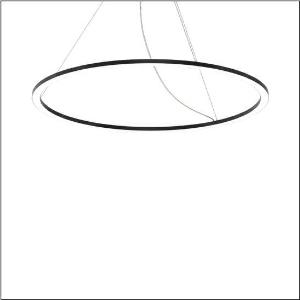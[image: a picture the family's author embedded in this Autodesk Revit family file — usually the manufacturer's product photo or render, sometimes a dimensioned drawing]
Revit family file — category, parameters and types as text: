
# Revit family: silica_r__21_ring-d_5pjbd4d1104a_1e9f
name_source: partatom
category: Lighting Fixtures
units: mm (PartAtom-declared; Revit-internal decimal feet)

## family parameters
Cut with Voids When Loaded = No
Host = Face
Light Source = No
Part Type = Normal
Room Calculation Point = No
Round Connector Dimension = Use Diameter
Shared = No

## types (1)
- Silica® 21 Ring-D (1 x LED, 10840 lm, 125 W, 3000K)
    Apparent Load = 125 VA
    CIE Flux Codes = 37 69 92 100 100
    Color Rendering = 80
    Color Temperature = 3000K
    Default Elevation = 1800 mm
    Description = Silica® 21 Ring-D, suspended luminaire, of PMMA, frosted, light emission: ring underside luminous distribution, primary light characteristic: symmetric, installation type: suspended mounting, LED, rated luminous flux: 10.840lm, luminous efficacy: 87lm/W, light colour: 830, colour temperature: 3000K, with terminal, 5-pole, mains connection: 230V, AC/DC, 0/50..60Hz, rated input power: 125W, housing, of extruded aluminium section, jet black (RAL 9005), diameter: 1.450mm, ceiling canopy, jet black (RAL 9005), protection rating (lamp compartment): IP40, insulation class (complete): insulation class I (protective earthing), certification: CE, impact resistance: IK02, permissible operating ambient temperature: 0..+35°C, packaging unit: 1 piece
    Height = 25 mm  [stored 0.082021 ft]
    Lamp = 1 x LED
    Lamp Light Flux = 10840 lm
    Lamp Power = 125 W
    Lamp count = 1
    Length = 1450 mm
    Luminous efficacy = 87 lm/W
    Manufacturer = Siteco
    ModVariant = No
    Model = 5PJBD4D1104A
    Mounting Place = Ceiling
    Mounting Type = Pendant
    Number of Poles = 1
    OnlyDefault = Yes
    Power Factor = 1
    Product Name = Silica® 21 Ring-D
    Product group = suspended luminaire
    ProductGroupID = 904
    Protection Class = Protection class I
    Protection Degree = Degree of protection
    RLX_Detail_Level = 1
    RLX_Emergency_Light_Flux = 0 lm
    RLX_Emergency_Type = 0
    RLX_Emergency_Type_DB = No
    RlxData = <blob elided: 19381 chars, md5=9b381cd4>
    Socket = socket
    Standby Power = 0 W
    System Light Flux = 10840 lm
    System Power = 125 W
    Type Comments = Product without accessories
    Type Image = l_1258357.jpg
    URL = http://relux.com
    VarID = ---
    Voltage = 0 V
    Weight = 0.00 kg
    Width = 0 mm  [stored 0 ft]

note: [stored X ft] marks values corroborated as IEEE doubles in the binary element streams (Revit-internal decimal feet)

## geometry (parser evidence)
native form markers: Blend x4, Sweep x10
no freeform markers — native parametric forms only
